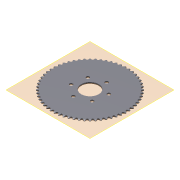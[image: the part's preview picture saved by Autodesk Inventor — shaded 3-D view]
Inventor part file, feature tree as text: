
AUTODESK INVENTOR PART (.ipt)
format: ipt  version: 2011 (Build 150239000, 239)  size: 1,379,840 bytes
history: native  units: mm
features: other x6, extrude x3, sketch x2, pattern_linear x1, pattern_circular x1, hole x1
ambient origin geometry x8: Origin, YZ Plane, XZ Plane, XY Plane, X Axis, Y Axis, Z Axis, Center Point
bodies: Solid1 (feature_tree)
feature tree (14):
  other  "Theoretical Tooth Profile"
  other  "Tooth Profile"
  other  "Section Profile"
  other  "Shroud"
  other  "Strand"
  pattern_linear  "Strand Pattern"  Spacing1=1.6665mm  [1 undecoded]
  extrude  "Theoretical Tooth"  Depth=21.991149mm
  extrude  "Tooth"  Depth=2.978695mm
  pattern_circular  "Tooth Pattern"  [2 undecoded]
  other  "Timing Plane"
  extrude  "Extrusion4"  Depth=4.3065mm
  hole  "Hole1"  [1 undecoded]
  sketch  "Sketch4"  dims[d0=121.331499mm]
  sketch  "Sketch5"  dims[d2=1.047198mm d3=1.6665mm d10=21.991149mm d11=2.978695mm d12=2.64mm d13=4.3065mm d14=4.62mm d18=10.0mm d19=0.0mm d20=600.0mm d21=360.0deg d23=1.905mm d28=0.0mm d29=0.0mm d30=2.286mm d31=106.796418mm d32=2.286mm d33=0.8255mm d34=6.35mm d36=90.0deg d37=90.0deg d38=10.0mm d40=6.4mm d42=0.0mm d43=1.143mm d44=24.172811mm d45=1.6665mm d46=24.552mm d47=0.0mm d48=25.4mm d49=0.0mm d50=10.0mm d51=28.575mm d52=25.4mm d53=0.0mm d54=23.8125mm d55=60.0mm d57=360.0deg d59=5.2324mm d60=19.05mm d61=9.525mm d62=6.35mm d63=14.3117mm d64=25.4mm d65=20.594885mm]
note: 4 required parameter values undecoded (feature->parameter linkage not recoverable at this tier; creation-order binding heuristic only, values carry confidence <= 0.55)
